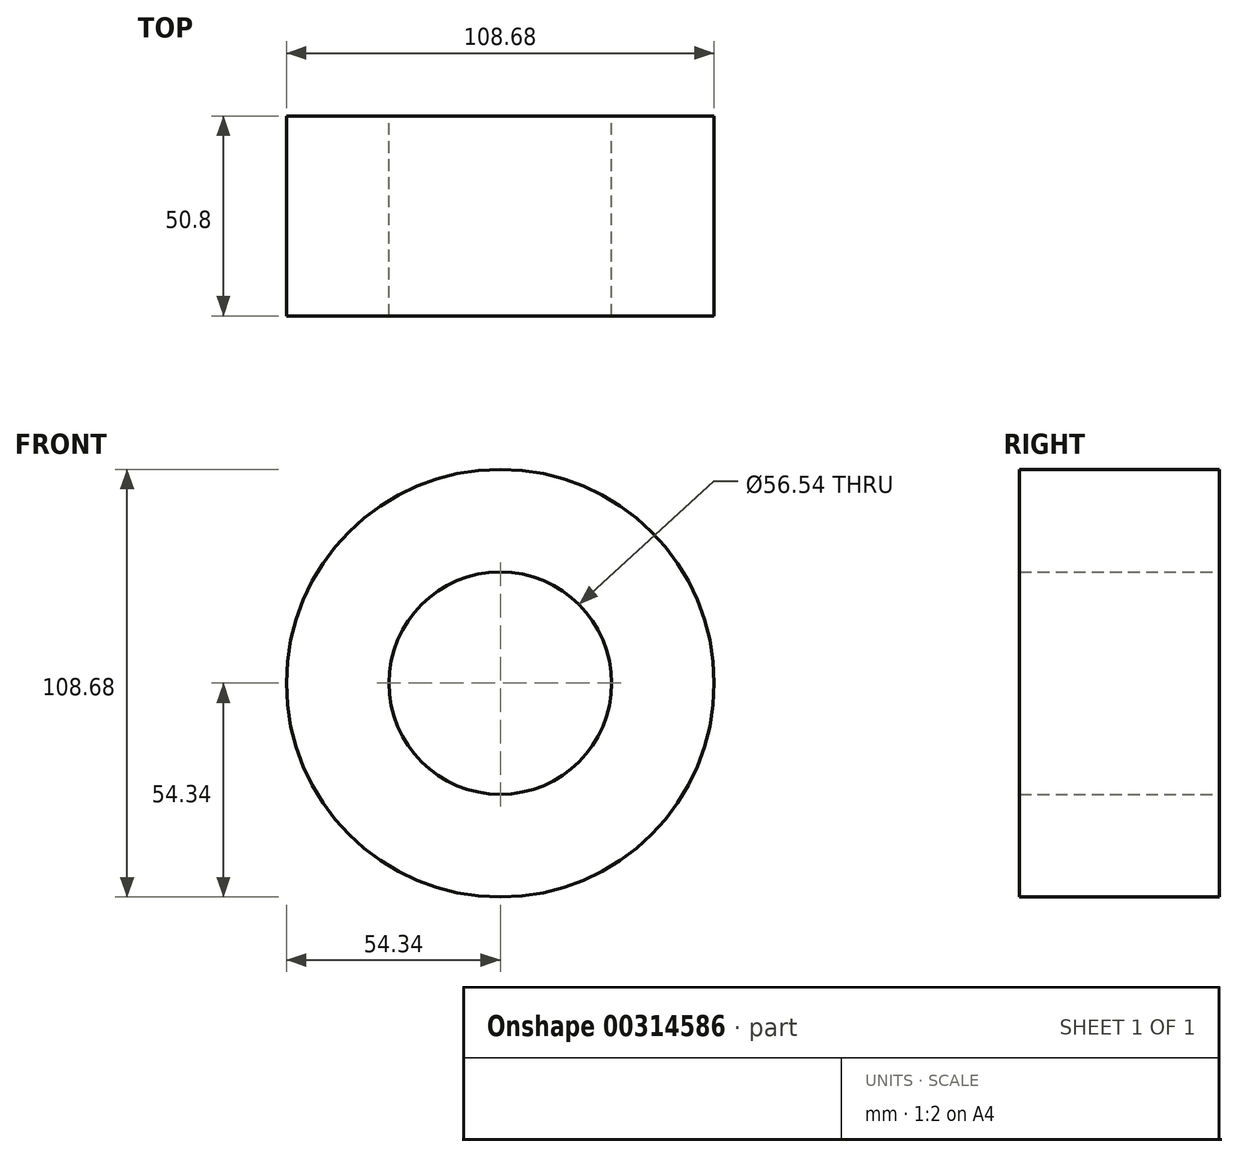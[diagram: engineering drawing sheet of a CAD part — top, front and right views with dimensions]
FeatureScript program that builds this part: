
annotation { "Feature Type Name" : "Feature", "Feature Type Description" : "" }
export const myFeature = defineFeature(function(context is Context, id is Id, definition is map)
    precondition{}
    {
        {
            var Q0;
            Q0=qCreatedBy(makeId("Front.planeOp"),FACE);
            var sketch = newSketch(context, id + "F0", { "sketchPlane" : qUnion([Q0])});
            skCircle(sketch, "E0", {"center": v(0, 0) * mm, "radius": 54.34 * mm});
            skCircle(sketch, "E1", {"center": v(0, 0) * mm, "radius": 28.27 * mm});
            skSolve(sketch);
        }
        {
            var Q0;
            Q0=makeQuery(id+"F0.imprint","IMPRINT",FACE,{"disambiguationData":[TD([[makeQuery(id+"F0.imprint","IMPRINT",EDGE,{"derivedFrom":sQuery(id+"F0.wireOp",EDGE,"E0")}),1.0]])]});
            extrude(context, id + "F1", {"entities" : qUnion([Q0]), "depth" : 25.4 * mm, "hasSecondDirection" : true, "secondDirectionOppositeDirection" : true, "secondDirectionDepth" : 25.4 * mm});
        }
    });
